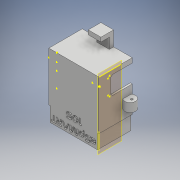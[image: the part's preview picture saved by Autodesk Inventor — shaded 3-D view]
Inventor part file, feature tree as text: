
AUTODESK INVENTOR PART (.ipt)
format: ipt  version: 2018.3 (Build 223284000, 284)  size: 761,856 bytes
history: native  units: mm
features: other x56, sketch x48, extrude x16, split x4, chamfer x4, shell x2, plane x1
ambient origin geometry x8: Origin, YZ Plane, XZ Plane, XY Plane, X Axis, Y Axis, Z Axis, Center Point
bodies: Body1 (feature_tree), Body2 (feature_tree), Body3 (feature_tree)
feature tree (131):
  other  "Sólido1"
  extrude  "Extrusión1"  Depth=17.6mm
  sketch  "Boceto2"  dims[d2=0.9mm d3=0.0mm d6=2.4mm d7=0.0mm d8=0.9mm]
  extrude  "Extrusión2"  Depth=0.9mm TaperAngle=0.0deg
  shell  "Vaciado1"  Thickness=0.9mm
  sketch  "Boceto4"  dims[d11=3.3mm d12=8.0mm d13=0.0mm]
  sketch  "Boceto5"  dims[d14=8.0mm d15=0.0mm d16=8.0mm d17=0.0mm]
  extrude  "Extrusión3"  Depth=3.3mm
  sketch  "Boceto7"  dims[d21=2.0mm]
  sketch  "Boceto8"  dims[d22=24.5mm]
  sketch  "Boceto9"  dims[d23=7.9mm d24=10.4mm d25=0.0mm]
  sketch  "Boceto10"  dims[d26=2.0mm]
  sketch  "Boceto11"  dims[d27=2.0mm]
  sketch  "Boceto12"  dims[d28=2.9mm]
  extrude  "Extrusión4"  Depth=3.3mm TaperAngle=0.0deg
  extrude  "Extrusión5"  Depth=8.0mm TaperAngle=0.0deg
  other  "Engrosado1"
  other  "Engrosado2"
  sketch  "Boceto15"  dims[d31=0.4mm]
  extrude  "Extrusión6"  Depth=2.0mm
  other  "Engrosado3"
  other  "Engrosado4"
  other  "Engrosado5"
  other  "Engrosado6"
  other  "Engrosado7"
  shell  "Vaciado2"  Thickness=2.0mm
  other  "Engrosado8"
  other  "Engrosado9"
  other  "Engrosado10"
  other  "Engrosado11"
  other  "Engrosado12"
  other  "Engrosado13"
  other  "Engrosado14"
  other  "Engrosado15"
  other  "Engrosado16"
  sketch  "Boceto17"  dims[d33=0.4mm]
  plane  "Plano de trabajo1"
  sketch  "Boceto18"  dims[d34=0.4mm]
  sketch  "Boceto19"  dims[d35=0.4mm]
  other  "Forma1"
  split  "Dividir1"
  other  "Engrosado17"
  other  "Engrosado18"
  other  "Engrosado19"
  other  "Engrosado20"
  other  "Engrosado21"
  other  "Suprimir cara1"
  other  "Combinar1"
  other  "Engrosado22"
  other  "Engrosado23"
  chamfer  "Chaflán1"  Distance=10.4mm
  chamfer  "Chaflán2"  Distance=1.0mm
  sketch  "Boceto20"  dims[d36=0.9mm]
  sketch  "Boceto21"  dims[d37=0.4mm]
  other  "Reemplazar cara1"
  other  "Reemplazar cara2"
  other  "Engrosado24"
  other  "Engrosado25"
  other  "Engrosado26"
  chamfer  "Chaflán3"  Distance=1.0mm
  chamfer  "Chaflán4"  Distance=1.0mm
  sketch  "Boceto22"  dims[d38=0.4mm]
  sketch  "Boceto23"  dims[d39=0.4mm]
  sketch  "Boceto24"  dims[d40=0.4mm]
  sketch  "Boceto25"  dims[d41=0.9mm]
  other  "Repujado2"
  other  "Engrosado27"
  extrude  "Extrusión8"  Depth=2.0mm
  other  "Engrosado29"
  extrude  "Extrusión10"  Depth=0.8mm TaperAngle=45.0deg
  split  "Dividir2"
  other  "Engrosado30"
  sketch  "Boceto33"  dims[d44=1.5mm]
  extrude  "Extrusión12"  Depth=0.8mm TaperAngle=45.0deg
  extrude  "Extrusión13"  Depth=1.5mm
  other  "Engrosado31"
  sketch  "Boceto37"  dims[d47=0.6mm]
  other  "Engrosado32"
  other  "Engrosado33"
  sketch  "Boceto38"  dims[d48=0.6mm]
  other  "Engrosado34"
  other  "Engrosado35"
  sketch  "Boceto39"  dims[d49=0.2mm]
  sketch  "Boceto40"  dims[d50=0.2mm]
  other  "Engrosado36"
  sketch  "Boceto41"  dims[d51=0.6mm]
  extrude  "Extrusión14"  Depth=1.5mm
  split  "Dividir3"
  other  "Engrosado37"
  split  "Dividir4"
  other  "Engrosado38"
  other  "Engrosado39"
  other  "Engrosado40"
  other  "Engrosado41"
  other  "Engrosado42"
  other  "Engrosado43"
  sketch  "Boceto45"  dims[d58=0.9mm]
  extrude  "Extrusión17"  Depth=2.0mm
  other  "Engrosado44"
  other  "Engrosado45"
  other  "Engrosado46"
  extrude  "Extrusión19"  Depth=2.0mm
  extrude  "Extrusión20"  Depth=2.0mm
  extrude  "Extrusión21"  Depth=2.0mm
  other  "Engrosado47"
  other  "Engrosado48"
  sketch  "Sketch51"  dims[d62=0.1mm]
  sketch  "Sketch52"  dims[d63=0.1mm]
  sketch  "Sketch53"  dims[d64=0.2mm]
  sketch  "Sketch54"  dims[d65=0.2mm]
  sketch  "Sketch55"  dims[d66=0.9mm]
  extrude  "Extrusion22"  Depth=0.8mm TaperAngle=45.0deg
  sketch  "Boceto1"  dims[d0=16.1mm d1=17.6mm]
  sketch  "Boceto3"  dims[d9=3.3mm d10=2.9mm]
  sketch  "Boceto6"  dims[d18=2.0mm d19=2.0mm d20=2.0mm]
  sketch  "Boceto13"  dims[d29=2.9mm]
  sketch  "Boceto14"  dims[d30=0.4mm]
  sketch  "Boceto16"  dims[d32=0.4mm]
  other  "Sólido2"
  sketch  "Boceto30"  dims[d42=0.9mm]
  sketch  "Boceto31"  dims[d43=1.5mm]
  sketch  "Boceto34"  dims[d45=0.8mm]
  sketch  "Boceto36"  dims[d46=0.8mm]
  sketch  "Boceto42"  dims[d52=0.6mm]
  sketch  "Boceto43"  dims[d53=0.6mm]
  sketch  "Boceto44"  dims[d54=0.6mm]
  sketch  "Boceto47"  dims[d59=0.9mm]
  sketch  "Boceto49"  dims[d60=0.8mm]
  sketch  "Boceto50"  dims[d61=0.8mm]
  sketch  "Sketch56"  dims[d67=0.9mm d68=1.0mm d69=1.0mm d70=1.0mm d71=1.0mm d72=0.8mm d73=2.0mm d74=45.0deg d75=0.8mm d76=2.0mm d77=45.0deg d78=1.5mm d79=1.5mm d80=0.3mm d81=0.3mm d82=0.3mm d83=0.3mm d84=0.8mm d85=2.0mm d86=45.0deg d87=0.8mm d88=2.0mm d89=45.0deg d92=0.7mm d93=0.0mm d94=4.25mm d95=4.25mm d105=11.6mm d106=0.0mm d107=7.3mm d108=7.3mm d114=11.6mm d115=0.0mm d116=7.3mm d117=7.3mm d121=1.0mm d122=4.3mm d123=0.0mm d124=1.0mm d125=4.3mm d126=0.0mm d127=1.2mm d128=1.2mm d129=7.3mm d130=7.3mm d131=7.3mm d132=7.3mm d133=1.3mm d134=7.3mm d135=7.3mm d136=7.3mm d137=7.3mm d138=7.3mm d139=7.3mm d140=2.5mm d141=8.7mm d142=0.0mm d143=4.4mm d144=4.4mm d145=1.0mm d146=4.4mm d147=4.4mm d148=0.1mm d149=0.1mm d150=0.1mm d151=0.1mm d152=0.1mm d153=0.1mm d154=0.1mm d155=0.1mm d156=0.2mm d157=0.2mm d158=11.25mm d159=3.0mm d160=3.0mm d167=11.85mm d168=3.0mm d169=3.0mm d171=7.0mm d172=0.0mm d176=0.1mm d177=0.1mm d178=0.1mm d179=0.1mm d180=0.1mm d181=0.1mm d182=2.0mm d183=2.0mm d184=4.0mm d185=0.0mm d186=2.0mm d187=7.0mm d188=0.0mm d189=2.0mm d190=4.0mm d191=0.0mm d192=0.1mm d193=0.1mm d194=0.1mm d195=0.1mm d196=3.7mm d197=1.4mm d198=2.0mm d199=0.0mm]
  other  "Sup1"
